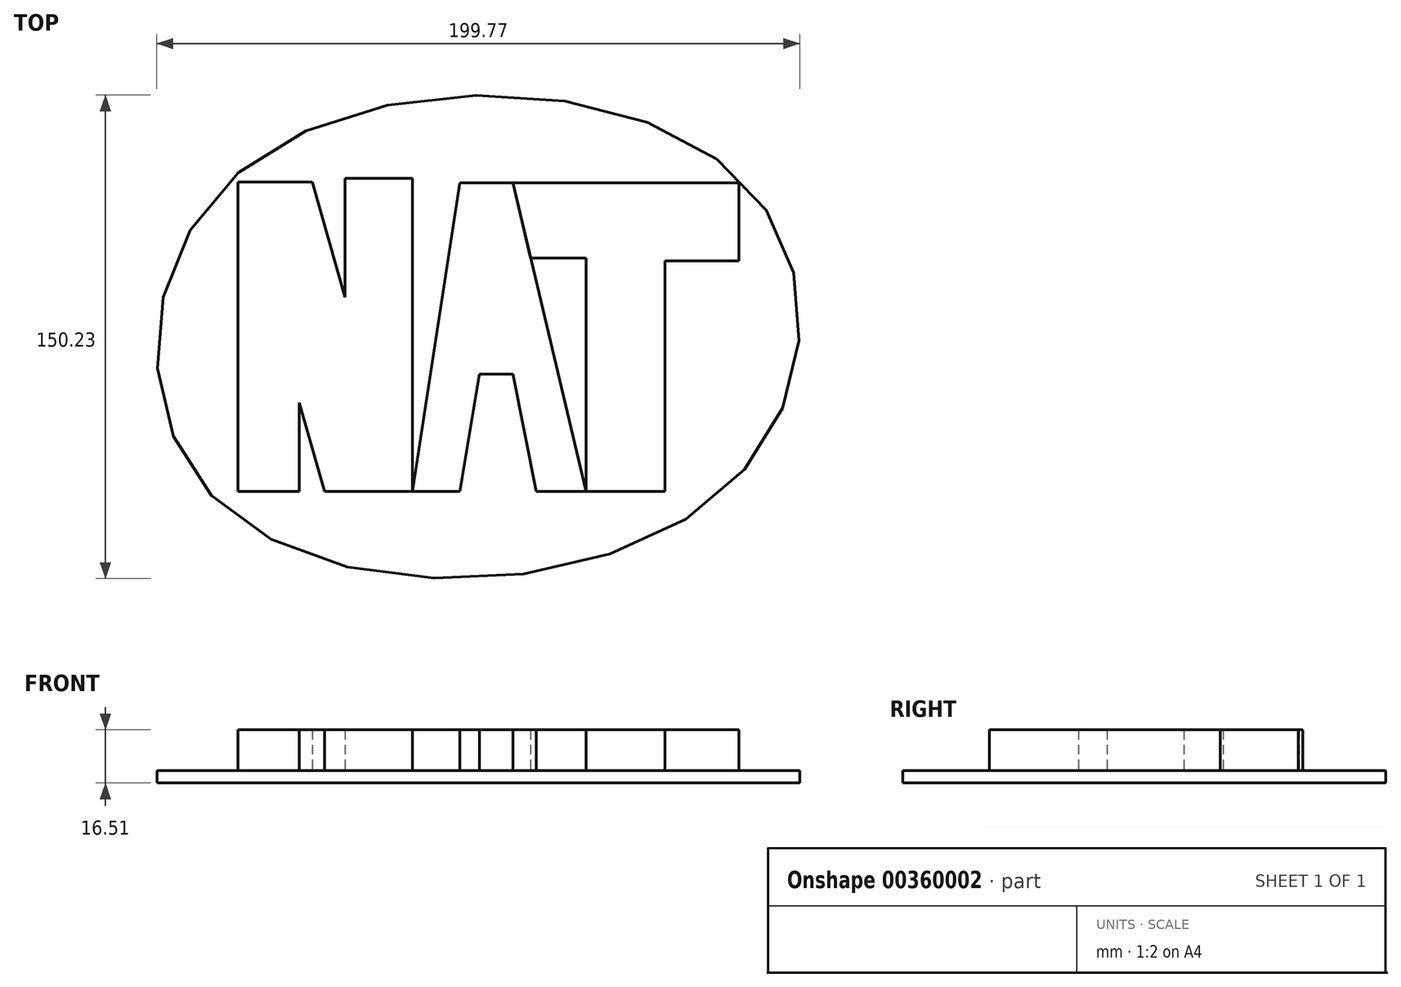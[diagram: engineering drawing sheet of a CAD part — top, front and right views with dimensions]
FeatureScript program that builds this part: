
annotation { "Feature Type Name" : "Feature", "Feature Type Description" : "" }
export const myFeature = defineFeature(function(context is Context, id is Id, definition is map)
    precondition{}
    {
        {
            var Q0;
            Q0=qCreatedBy(makeId("Top.planeOp"),FACE);
            var sketch = newSketch(context, id + "F0", { "sketchPlane" : qUnion([Q0])});
            skLineSegment(sketch, "E0", {"start": v(-85.4, 46.78) * mm, "end": v(-85.4, -49.4) * mm});
            skLineSegment(sketch, "E1", {"start": v(-85.4, 46.78) * mm, "end": v(-62.38, 46.78) * mm});
            skLineSegment(sketch, "E2", {"start": v(-62.38, 46.78) * mm, "end": v(-52.17, 11.01) * mm});
            skLineSegment(sketch, "E3", {"start": v(-85.4, -49.4) * mm, "end": v(-66.46, -49.4) * mm});
            skLineSegment(sketch, "E4", {"start": v(-66.46, -49.4) * mm, "end": v(-66.46, -21.8) * mm});
            skLineSegment(sketch, "E5", {"start": v(-66.46, -21.8) * mm, "end": v(-58.58, -49.4) * mm});
            skLineSegment(sketch, "E6", {"start": v(-58.58, -49.4) * mm, "end": v(-31.19, -49.4) * mm});
            skLineSegment(sketch, "E7", {"start": v(-31.19, -49.4) * mm, "end": v(-31.19, 47.95) * mm});
            skLineSegment(sketch, "E8", {"start": v(-52.17, 11.01) * mm, "end": v(-52.17, 47.94) * mm});
            skLineSegment(sketch, "E9", {"start": v(-52.17, 47.94) * mm, "end": v(-31.19, 47.95) * mm});
            skLineSegment(sketch, "E10", {"start": v(-31.19, -49.4) * mm, "end": v(-16.53, 46.5) * mm});
            skLineSegment(sketch, "E11", {"start": v(-16.53, 46.5) * mm, "end": v(0, 46.5) * mm});
            skLineSegment(sketch, "E12", {"start": v(0, 46.5) * mm, "end": v(22.74, -49.4) * mm});
            skLineSegment(sketch, "E13", {"start": v(22.74, -49.4) * mm, "end": v(7.27, -49.4) * mm});
            skLineSegment(sketch, "E14", {"start": v(7.27, -49.4) * mm, "end": v(0, -12.94) * mm});
            skLineSegment(sketch, "E15", {"start": v(0, -12.94) * mm, "end": v(-10.4, -12.94) * mm});
            skLineSegment(sketch, "E16", {"start": v(-10.4, -12.94) * mm, "end": v(-16.53, -49.4) * mm});
            skLineSegment(sketch, "E17", {"start": v(-16.53, -49.4) * mm, "end": v(-31.19, -49.4) * mm});
            skLineSegment(sketch, "E18", {"start": v(0, 46.5) * mm, "end": v(70.25, 46.5) * mm});
            skLineSegment(sketch, "E19", {"start": v(70.25, 46.5) * mm, "end": v(70.25, 22.3) * mm});
            skLineSegment(sketch, "E20", {"start": v(70.25, 22.3) * mm, "end": v(47.22, 22.3) * mm});
            skLineSegment(sketch, "E21", {"start": v(47.22, 22.3) * mm, "end": v(47.22, -49.4) * mm});
            skLineSegment(sketch, "E22", {"start": v(47.22, -49.4) * mm, "end": v(22.74, -49.4) * mm});
            skLineSegment(sketch, "E23", {"start": v(22.74, -49.4) * mm, "end": v(22.74, 23.17) * mm});
            skLineSegment(sketch, "E24", {"start": v(22.74, 23.17) * mm, "end": v(5.53, 23.17) * mm});
            skSolve(sketch);
        }
        {
            var Q0;
            Q0=makeQuery(id+"F0.imprint","IMPRINT",FACE,{"disambiguationData":[TD([[makeQuery(id+"F0.imprint","IMPRINT",EDGE,{"derivedFrom":sQuery(id+"F0.wireOp",EDGE,"E0")}),1.0]])]});
            extrude(context, id + "F1", {"entities" : qUnion([Q0]), "depth" : 12.7 * mm});
        }
        {
            var Q0;
            Q0=makeQuery(id+"F0.imprint","IMPRINT",FACE,{"disambiguationData":[TD([[makeQuery(id+"F0.imprint","IMPRINT",EDGE,{"derivedFrom":sQuery(id+"F0.wireOp",EDGE,"E10")}),-1.0]])]});
            extrude(context, id + "F2", {"entities" : qUnion([Q0]), "depth" : 12.7 * mm});
        }
        {
            var Q0;
            {var subQ0=sQuery(id+"F0.wireOp",EDGE,"E18");Q0=makeQuery(id+"F0.imprint","IMPRINT",FACE,{"disambiguationData":[TD([[makeQuery(id+"F0.imprint","IMPRINT",EDGE,{"derivedFrom":subQ0}),-1.0]])]});}
            extrude(context, id + "F3", {"entities" : qUnion([Q0]), "depth" : 12.7 * mm});
        }
        {
            var Q0;
            Q0=qCreatedBy(makeId("Top.planeOp"),FACE);
            var sketch = newSketch(context, id + "F4", { "sketchPlane" : qUnion([Q0])});
            skFitSpline(sketch, "E25", {"points": [v(-85.4, 49.64) * mm, v(69.74, 48.66) * mm, v(64.85, -49.76) * mm, v(-90.6, -53.67) * mm, v(-85.4, 49.64) * mm]});
            skSolve(sketch);
        }
        {
            var Q0;
            Q0=makeQuery(id+"F4.imprint","IMPRINT",FACE,{"disambiguationData":[TD([[makeQuery(id+"F4.imprint","IMPRINT",EDGE,{"derivedFrom":sQuery(id+"F4.wireOp",EDGE,"E25")}),-1.0]])]});
            extrude(context, id + "F5", {"entities" : qUnion([Q0]), "oppositeDirection" : true, "depth" : 3.8 * mm});
        }
    });
